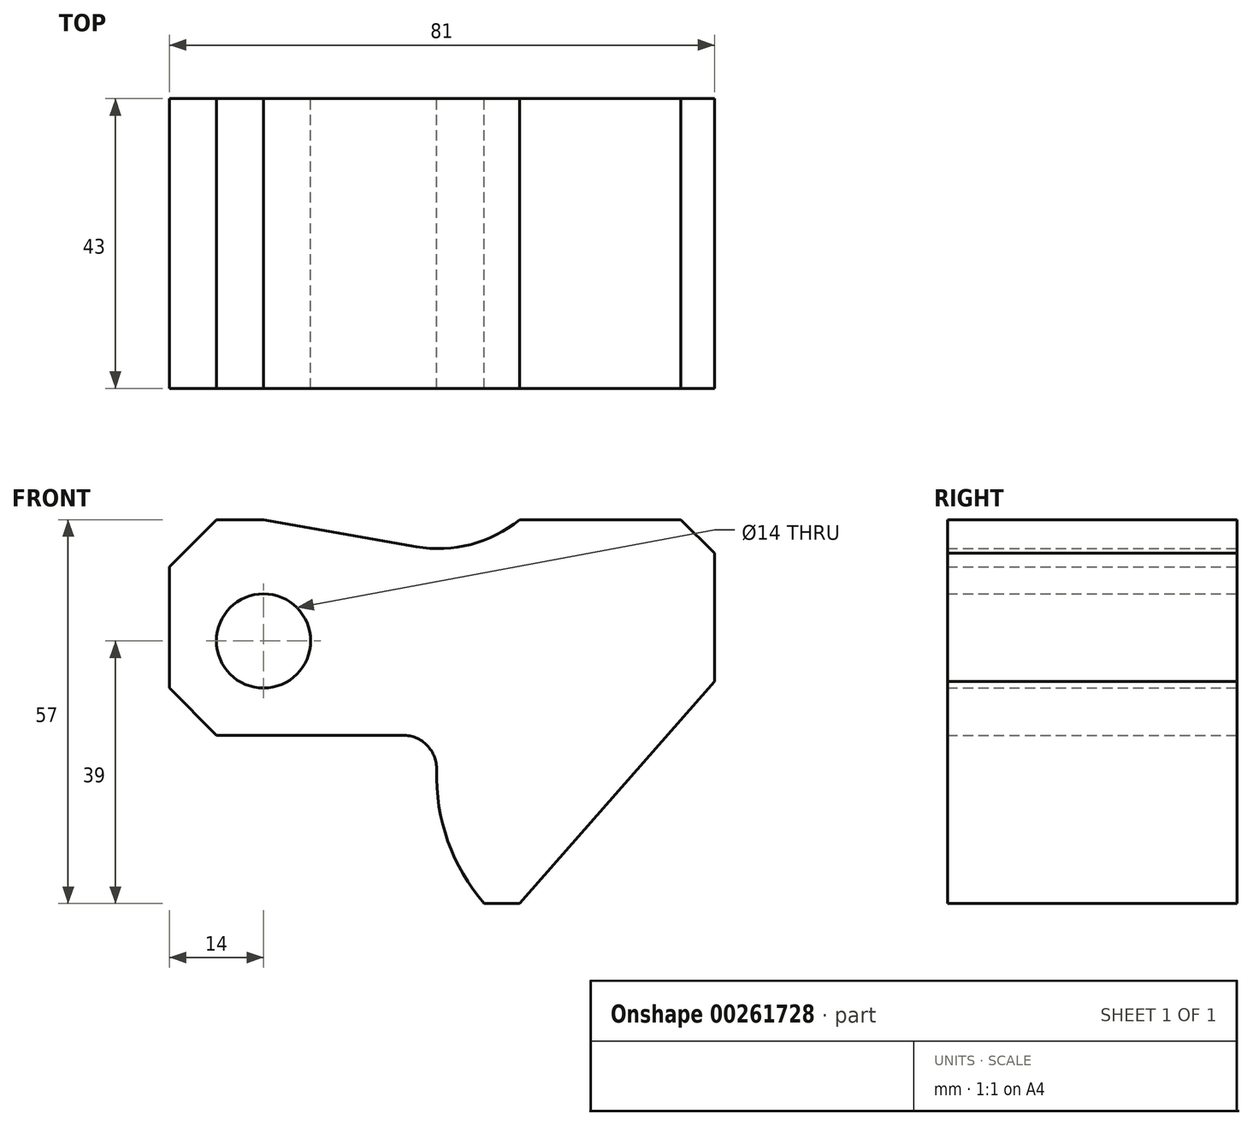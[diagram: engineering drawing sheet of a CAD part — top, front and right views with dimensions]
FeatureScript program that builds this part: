
annotation { "Feature Type Name" : "Feature", "Feature Type Description" : "" }
export const myFeature = defineFeature(function(context is Context, id is Id, definition is map)
    precondition{}
    {
        {
            var Q0;
            Q0=qCreatedBy(makeId("Front.planeOp"),FACE);
            var sketch = newSketch(context, id + "F0", { "sketchPlane" : qUnion([Q0])});
            skCircle(sketch, "E0", {"center": v(0, 0) * mm, "radius": 7 * mm});
            skLineSegment(sketch, "E1", {"start": v(0, 18) * mm, "end": v(-7, 18) * mm});
            skLineSegment(sketch, "E2", {"start": v(-7, 18) * mm, "end": v(-14, 11) * mm});
            skLineSegment(sketch, "E3", {"start": v(-14, 11) * mm, "end": v(-14, 29.6) * mm, "construction": true});
            skLineSegment(sketch, "E4", {"start": v(0, -14) * mm, "end": v(-7, -14) * mm});
            skLineSegment(sketch, "E5", {"start": v(-7, -14) * mm, "end": v(-14, -7) * mm});
            skLineSegment(sketch, "E6", {"start": v(-14, -7) * mm, "end": v(-14, -41.1) * mm, "construction": true});
            skLineSegment(sketch, "E7", {"start": v(-14, 11) * mm, "end": v(-14, -7) * mm});
            skLineSegment(sketch, "E8", {"start": v(38, 18) * mm, "end": v(62, 18) * mm});
            skLineSegment(sketch, "E9", {"start": v(12.13, 15.86) * mm, "end": v(0, 18) * mm});
            skLineSegment(sketch, "E10", {"start": v(0, 18) * mm, "end": v(38, 18) * mm, "construction": true});
            skLineSegment(sketch, "E11", {"start": v(12.13, 15.86) * mm, "end": v(22.68, 14) * mm});
            skArc(sketch, "E12", {"start": v(22.68, 14) * mm, "mid": v(30.78, 14.33) * mm, "end": v(38, 18) * mm});
            skLineSegment(sketch, "E13", {"start": v(62, 18) * mm, "end": v(67, 13) * mm});
            skLineSegment(sketch, "E14", {"start": v(67, 13) * mm, "end": v(67, 30.47) * mm, "construction": true});
            skLineSegment(sketch, "E15", {"start": v(67, 13) * mm, "end": v(67, -6) * mm});
            skLineSegment(sketch, "E16", {"start": v(38, -39) * mm, "end": v(32.79, -39) * mm});
            skLineSegment(sketch, "E17", {"start": v(38, -39) * mm, "end": v(67, -6) * mm});
            skArc(sketch, "E18", {"start": v(25.7, -19.15) * mm, "mid": v(27.38, -29.74) * mm, "end": v(32.79, -39) * mm});
            skLineSegment(sketch, "E19", {"start": v(0, -14) * mm, "end": v(20.71, -14) * mm});
            skArc(sketch, "E20", {"start": v(25.7, -19.15) * mm, "mid": v(24.3, -15.52) * mm, "end": v(20.71, -14) * mm});
            skSolve(sketch);
        }
        {
            var Q0;
            Q0 = qSketchRegion(id + "F0", true);
            extrude(context, id + "F1", {"entities" : qUnion([Q0]), "endBound" : BoundingType.SYMMETRIC, "depth" : 43 * mm});
        }
    });
